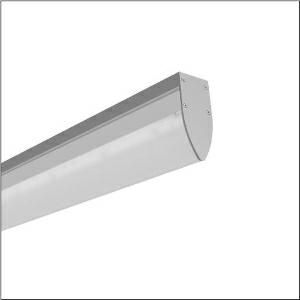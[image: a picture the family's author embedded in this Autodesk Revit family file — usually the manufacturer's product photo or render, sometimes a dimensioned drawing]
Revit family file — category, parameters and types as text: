
# Revit family: mira_21_td_51fr527g454a
name_source: partatom
category: Lighting Fixtures
units: mm (PartAtom-declared; Revit-internal decimal feet)

## family parameters
Cut with Voids When Loaded = No
Host = Face
Light Source = No
Part Type = Normal
Room Calculation Point = No
Round Connector Dimension = Use Diameter
Shared = No

## types (1)
- Mira 21 TD (1 x LED, 5500 lm, 39 W, 4000K)
    Apparent Load = 39 VA
    CIE Flux Codes = 40 68 87 81 100
    Color Rendering = 80
    Color Temperature = 4000K
    Default Elevation = 1800 mm
    Description = Mira 21 TD, clean room luminaire, primary light control with reflector, primary optical cover: cover, of PMMA, frosted, light emission: direct distribution, primary light characteristic: symmetric, installation type: surface-mounted, LED, rated luminous flux: 5.500lm, luminous efficacy: 141lm/W, light colour: 840, colour temperature: 4000K, control gear: ON/OFF, with terminal, 3-pole, max. 2.5mm², mains connection: 230V, AC, 50/60Hz, rated input power: 39W, luminaire housing, of sheet steel, coated, pure white (RAL 9010), length: 900mm, width: 55mm, height: 120mm, protection rating (complete): IP43, insulation class (complete): insulation class I (protective earthing), certification: CE, UKCA, permissible operating ambient temperature: -5..+40°C, standard: EN 50419, packaging unit: 1 piece
    Height = 120 mm
    Lamp = 1 x LED
    Lamp Light Flux = 5500 lm
    Lamp Power = 39 W
    Lamp count = 1
    Length = 900 mm
    Luminous efficacy = 141 lm/W
    Manufacturer = Siteco
    ModVariant = No
    Model = 51FR527G454A
    Mounting Place = Ceiling
    Mounting Type = Surface mounted
    Number of Poles = 1
    OnlyDefault = Yes
    Power Factor = 1
    Product Name = Mira 21 TD
    Product group = clean room luminaire | ceiling mounted
    ProductGroupID = 306
    Protection Class = Protection class I
    Protection Degree = IP 43
    RLX_Detail_Level = 1
    RLX_Emergency_Light_Flux = 0 lm
    RLX_Emergency_Type = 0
    RLX_Emergency_Type_DB = No
    RlxData = <blob elided: 25125 chars, md5=4e68704b>
    Socket = socket
    Standby Power = 0 W
    System Light Flux = 5500 lm
    System Power = 39 W
    Type Comments = Product without accessories
    Type Image = l_1007115.jpg
    URL = http://relux.com
    VarID = ---
    Voltage = 0 V
    Weight = 0.00 kg
    Width = 55 mm

## geometry (parser evidence)
native form markers: Blend x4, Sweep x13
no freeform markers — native parametric forms only
